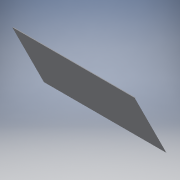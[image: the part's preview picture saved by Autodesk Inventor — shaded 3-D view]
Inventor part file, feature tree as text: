
AUTODESK INVENTOR PART (.ipt)
format: ipt  version: 2016 (Build 200138000, 138)  size: 103,936 bytes
history: native  units: mm
features: extrude x1, sketch x1
ambient origin geometry x8: Origin, YZ Plane, XZ Plane, XY Plane, X Axis, Y Axis, Z Axis, Center Point
bodies: Solid1 (feature_tree)
feature tree (2):
  extrude  "Extrusion1"  Depth=2.0mm
  sketch  "Sketch1"  dims[d0=462.0mm d1=2.0mm d2=90.0mm d3=0.0mm]
